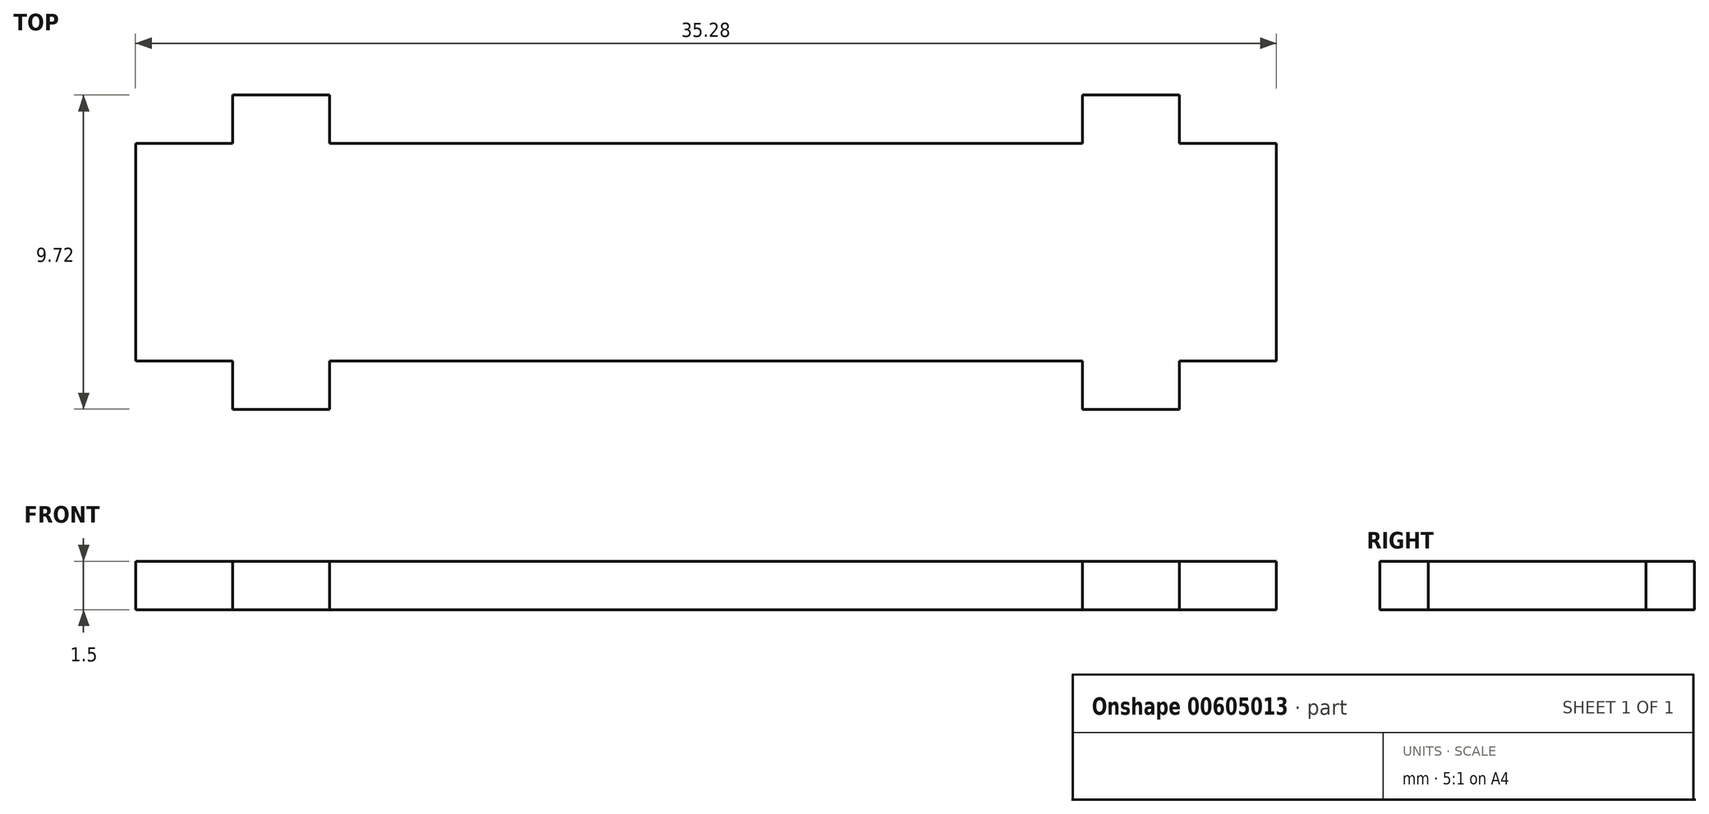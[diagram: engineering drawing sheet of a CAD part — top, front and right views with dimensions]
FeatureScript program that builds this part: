
annotation { "Feature Type Name" : "Feature", "Feature Type Description" : "" }
export const myFeature = defineFeature(function(context is Context, id is Id, definition is map)
    precondition{}
    {
        {
            var Q0;
            Q0=qCreatedBy(makeId("Top.planeOp"),FACE);
            var sketch = newSketch(context, id + "F0", { "sketchPlane" : qUnion([Q0])});
            skLineSegment(sketch, "E0.bottom", {"start": v(-17.64, 3.36) * mm, "end": v(17.64, 3.36) * mm});
            skLineSegment(sketch, "E0.top", {"start": v(-17.64, -3.36) * mm, "end": v(17.64, -3.36) * mm});
            skLineSegment(sketch, "E0.left", {"start": v(-17.64, 3.36) * mm, "end": v(-17.64, -3.36) * mm});
            skLineSegment(sketch, "E0.right", {"start": v(17.64, 3.36) * mm, "end": v(17.64, -3.36) * mm});
            skLineSegment(sketch, "E1.bottom", {"start": v(-14.64, 3.36) * mm, "end": v(-11.64, 3.36) * mm});
            skLineSegment(sketch, "E1.top", {"start": v(-14.64, 4.86) * mm, "end": v(-11.64, 4.86) * mm});
            skLineSegment(sketch, "E1.left", {"start": v(-14.64, 3.36) * mm, "end": v(-14.64, 4.86) * mm});
            skLineSegment(sketch, "E1.right", {"start": v(-11.64, 3.36) * mm, "end": v(-11.64, 4.86) * mm});
            skLineSegment(sketch, "E2.MirrorCS", {"start": v(14.64, 4.86) * mm, "end": v(11.64, 4.86) * mm});
            skLineSegment(sketch, "E3.MirrorCS", {"start": v(11.64, 3.36) * mm, "end": v(11.64, 4.86) * mm});
            skLineSegment(sketch, "E4.MirrorCS", {"start": v(14.64, 3.36) * mm, "end": v(14.64, 4.86) * mm});
            skLineSegment(sketch, "E5.MirrorCS", {"start": v(14.64, 3.36) * mm, "end": v(11.64, 3.36) * mm});
            skLineSegment(sketch, "E6.MirrorCS", {"start": v(-14.64, -4.86) * mm, "end": v(-11.64, -4.86) * mm});
            skLineSegment(sketch, "E7.MirrorCS", {"start": v(-11.64, -3.36) * mm, "end": v(-11.64, -4.86) * mm});
            skLineSegment(sketch, "E8.MirrorCS", {"start": v(-14.64, -3.36) * mm, "end": v(-14.64, -4.86) * mm});
            skLineSegment(sketch, "E9.MirrorCS", {"start": v(-14.64, -3.36) * mm, "end": v(-11.64, -3.36) * mm});
            skLineSegment(sketch, "E10.MirrorCS", {"start": v(14.64, -4.86) * mm, "end": v(11.64, -4.86) * mm});
            skLineSegment(sketch, "E11.MirrorCS", {"start": v(14.64, -3.36) * mm, "end": v(14.64, -4.86) * mm});
            skLineSegment(sketch, "E12.MirrorCS", {"start": v(14.64, -3.36) * mm, "end": v(11.64, -3.36) * mm});
            skLineSegment(sketch, "E13.MirrorCS", {"start": v(11.64, -3.36) * mm, "end": v(11.64, -4.86) * mm});
            skSolve(sketch);
        }
        {
            var Q0;
            Q0=qSketchRegion(id+"F0",true);
            extrude(context, id + "F1", {"entities" : qUnion([Q0]), "depth" : 1.5 * mm, "offsetDistance" : 25 * mm});
        }
    });
